# Revit family: Viega_ProPress 316_Ball Valve 4075
name_source: partatom
category: Pipe Accessories
units: mm (PartAtom-declared; Revit-internal decimal feet)

## family parameters
Always vertical = Yes
Cut with Voids When Loaded = No
OmniClass Number = 23.65.55.14.17
OmniClass Title = Adjusting/Controlling Valves for Liquid Services
Part Type = Valve - Breaks Into
Round Connector Dimension = Use Radius
Shared = No
Work Plane-Based = No

## types (1)
- 4075
    Assembly Code = D2090900
    Ball Material = Viega Stainless
    Body Material = Viega Stainless
    Connection Type = P x P
    Default Elevation = 0 mm  [stored 0 ft]
    Description = Ball Valve
    ENGworks Global = http://www.ENGworksGlobal.com
    Handle Cover Material = Viega Green
    Handle Material = Viega Metals
    K Coefficient = 0
    K Coefficient Table = Ball Valve Full Port Full Open
    Loss Method = K Coefficient from Table
    Manufacturer = Viega
    Maximum Working Pressure = 0.00 psi
    Maximum Working Temperature = 0 °F
    Model = 4075
    Part Count = 1
    Press End Material = Viega Stainless
    Product Page URL = http://bim.viega.us
    Series = ProPress 316
    Standards = See Catalog
    Stem Material = Viega Stainless
    URL = http://bim.viega.us
    V_Description = Ball Valve
    Version = 1

note: [stored X ft] marks values corroborated as IEEE doubles in the binary element streams (Revit-internal decimal feet)

## geometry (parser evidence)
native form markers: Sweep x11
no freeform markers — native parametric forms only
